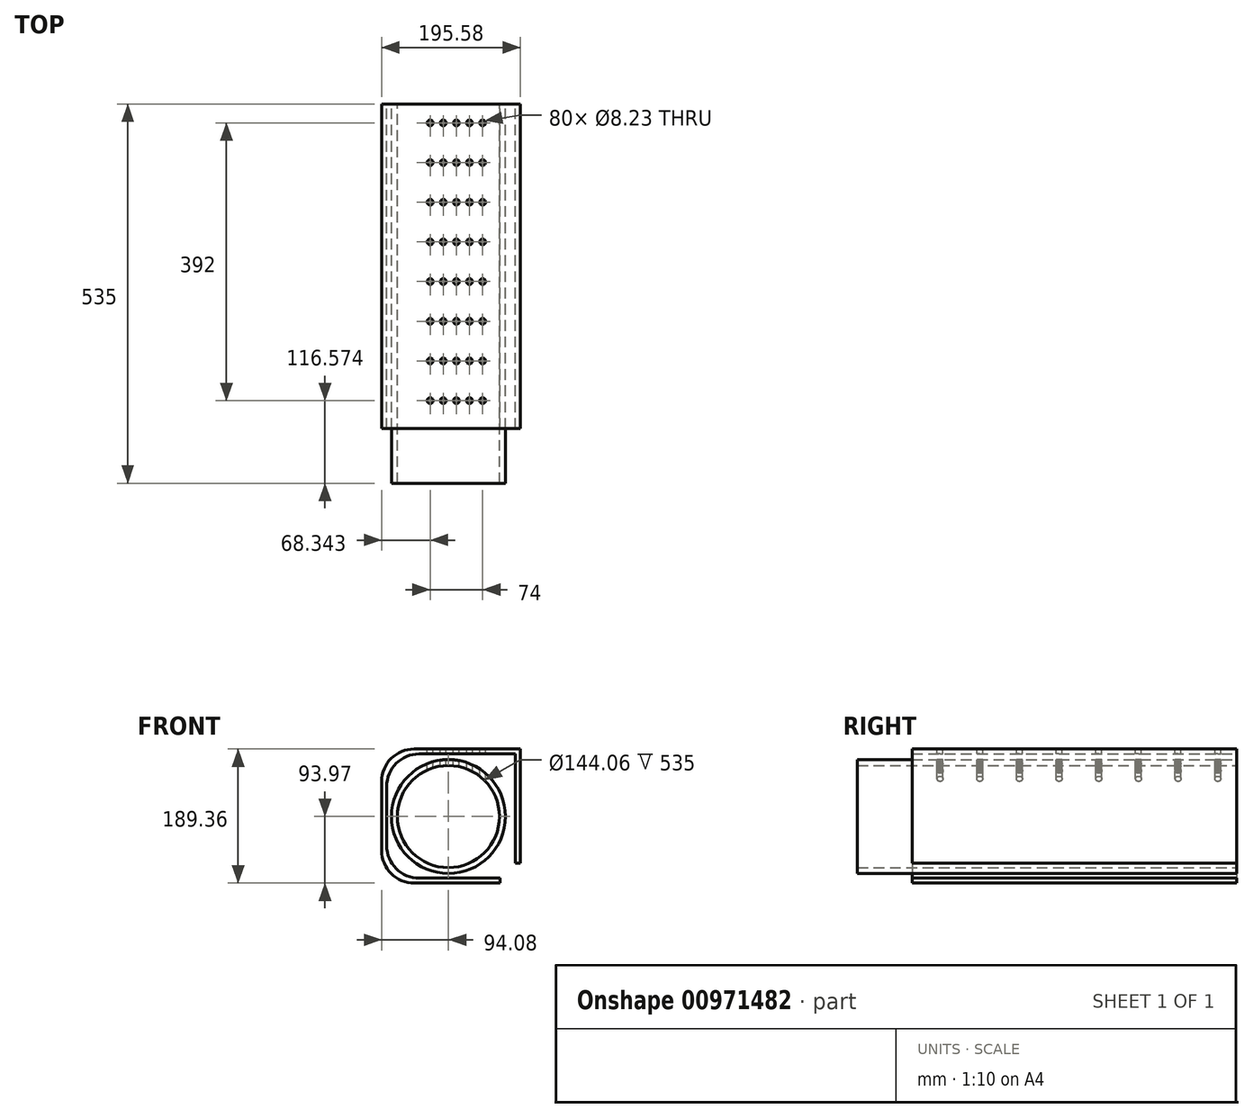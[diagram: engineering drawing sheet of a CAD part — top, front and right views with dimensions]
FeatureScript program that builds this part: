
annotation { "Feature Type Name" : "Feature", "Feature Type Description" : "" }
export const myFeature = defineFeature(function(context is Context, id is Id, definition is map)
    precondition{}
    {
        {
            var Q0;
            Q0=qCreatedBy(makeId("Front.planeOp"),FACE);
            var sketch = newSketch(context, id + "F0", { "sketchPlane" : qUnion([Q0])});
            skCircle(sketch, "E0", {"center": v(0, 0) * mm, "radius": 80.4 * mm});
            skCircle(sketch, "E1", {"center": v(0, 0) * mm, "radius": 72.03 * mm});
            skSolve(sketch);
        }
        {
            var Q0;
            Q0=makeQuery(id+"F0.imprint","IMPRINT",FACE,{"disambiguationData":[TD([[makeQuery(id+"F0.imprint","IMPRINT",EDGE,{"derivedFrom":sQuery(id+"F0.wireOp",EDGE,"E0")}),1.0]])]});
            extrude(context, id + "F1", {"entities" : qUnion([Q0]), "depth" : 535 * mm, "offsetDistance" : 25 * mm});
        }
        {
            var Q0;
            Q0=qCreatedBy(makeId("Front.planeOp"),FACE);
            var sketch = newSketch(context, id + "F2", { "sketchPlane" : qUnion([Q0])});
            skLineSegment(sketch, "E2.bottom", {"start": v(94.5, 88.4) * mm, "end": v(-87.08, 88.4) * mm});
            skLineSegment(sketch, "E2.top", {"start": v(94.5, -86.97) * mm, "end": v(-87.08, -86.97) * mm});
            skLineSegment(sketch, "E2.left", {"start": v(94.5, 88.4) * mm, "end": v(94.5, -86.97) * mm});
            skLineSegment(sketch, "E2.right", {"start": v(-87.08, 88.4) * mm, "end": v(-87.08, -86.97) * mm});
            skLineSegment(sketch, "E3.0", {"start": v(101.5, 95.4) * mm, "end": v(-94.08, 95.4) * mm});
            skLineSegment(sketch, "E3.1", {"start": v(101.5, 95.4) * mm, "end": v(101.5, -93.97) * mm});
            skLineSegment(sketch, "E3.2", {"start": v(101.5, -93.97) * mm, "end": v(-94.08, -93.97) * mm});
            skLineSegment(sketch, "E3.3", {"start": v(-94.08, 95.4) * mm, "end": v(-94.08, -93.97) * mm});
            skSolve(sketch);
        }
        {
            var Q0;
            Q0=makeQuery(id+"F2.imprint","IMPRINT",FACE,{"disambiguationData":[TD([[makeQuery(id+"F2.imprint","IMPRINT",EDGE,{"derivedFrom":sQuery(id+"F2.wireOp",EDGE,"E2.bottom")}),-1.0]])]});
            extrude(context, id + "F3", {"entities" : qUnion([Q0]), "depth" : 458 * mm, "offsetDistance" : 25 * mm});
        }
        {
            var Q0;
            Q0=makeQuery(id+"F3.opExtrude","SWEPT_EDGE",EDGE,{"disambiguationData":[OSD([sQuery(id+"F2.wireOp",EDGE,"E2.bottom"),sQuery(id+"F2.wireOp",EDGE,"E2.right")])]});
            var Q1;
            Q1=makeQuery(id+"F3.opExtrude","SWEPT_EDGE",EDGE,{"disambiguationData":[OSD([sQuery(id+"F2.wireOp",EDGE,"E3.0"),sQuery(id+"F2.wireOp",EDGE,"E3.3")])]});
            var Q2;
            Q2=makeQuery(id+"F3.opExtrude","SWEPT_EDGE",EDGE,{"disambiguationData":[OSD([sQuery(id+"F2.wireOp",EDGE,"E2.top"),sQuery(id+"F2.wireOp",EDGE,"E2.right")])]});
            var Q3;
            Q3=makeQuery(id+"F3.opExtrude","SWEPT_EDGE",EDGE,{"disambiguationData":[OSD([sQuery(id+"F2.wireOp",EDGE,"E3.2"),sQuery(id+"F2.wireOp",EDGE,"E3.3")])]});
            fillet(context, id + "F4", {"entities" : qUnion([Q0, Q1, Q2, Q3]), "radius" : 45.87 * mm, "tangentPropagation" : true, "allowEdgeOverflow" : false});
        }
        {
            var Q0;
            Q0=makeQuery(id+"F3.opExtrude","SWEPT_FACE",FACE,{"disambiguationData":[OSD([sQuery(id+"F2.wireOp",EDGE,"E3.0")])]});
            var sketch = newSketch(context, id + "F5", { "sketchPlane" : qUnion([Q0])});
            skCircle(sketch, "E4", {"center": v(-25.74, -26.43) * mm, "radius": 4.12 * mm});
            skCircle(sketch, "E5.0.1.0", {"center": v(-25.74, -82.43) * mm, "radius": 4.12 * mm});
            skCircle(sketch, "E5.0.2.0", {"center": v(-25.74, -138.43) * mm, "radius": 4.12 * mm});
            skCircle(sketch, "E5.0.3.0", {"center": v(-25.74, -194.43) * mm, "radius": 4.12 * mm});
            skCircle(sketch, "E5.0.4.0", {"center": v(-25.74, -250.43) * mm, "radius": 4.12 * mm});
            skCircle(sketch, "E5.0.5.0", {"center": v(-25.74, -306.43) * mm, "radius": 4.12 * mm});
            skCircle(sketch, "E5.0.6.0", {"center": v(-25.74, -362.43) * mm, "radius": 4.12 * mm});
            skCircle(sketch, "E5.0.7.0", {"center": v(-25.74, -418.43) * mm, "radius": 4.12 * mm});
            skCircle(sketch, "E5.1.0.0", {"center": v(-7.24, -26.43) * mm, "radius": 4.12 * mm});
            skCircle(sketch, "E5.1.1.0", {"center": v(-7.24, -82.43) * mm, "radius": 4.12 * mm});
            skCircle(sketch, "E5.1.2.0", {"center": v(-7.24, -138.43) * mm, "radius": 4.12 * mm});
            skCircle(sketch, "E5.1.3.0", {"center": v(-7.24, -194.43) * mm, "radius": 4.12 * mm});
            skCircle(sketch, "E5.1.4.0", {"center": v(-7.24, -250.43) * mm, "radius": 4.12 * mm});
            skCircle(sketch, "E5.1.5.0", {"center": v(-7.24, -306.43) * mm, "radius": 4.12 * mm});
            skCircle(sketch, "E5.1.6.0", {"center": v(-7.24, -362.43) * mm, "radius": 4.12 * mm});
            skCircle(sketch, "E5.1.7.0", {"center": v(-7.24, -418.43) * mm, "radius": 4.12 * mm});
            skCircle(sketch, "E5.2.0.0", {"center": v(11.26, -26.43) * mm, "radius": 4.12 * mm});
            skCircle(sketch, "E5.2.1.0", {"center": v(11.26, -82.43) * mm, "radius": 4.12 * mm});
            skCircle(sketch, "E5.2.2.0", {"center": v(11.26, -138.43) * mm, "radius": 4.12 * mm});
            skCircle(sketch, "E5.2.3.0", {"center": v(11.26, -194.43) * mm, "radius": 4.12 * mm});
            skCircle(sketch, "E5.2.4.0", {"center": v(11.26, -250.43) * mm, "radius": 4.12 * mm});
            skCircle(sketch, "E5.2.5.0", {"center": v(11.26, -306.43) * mm, "radius": 4.12 * mm});
            skCircle(sketch, "E5.2.6.0", {"center": v(11.26, -362.43) * mm, "radius": 4.12 * mm});
            skCircle(sketch, "E5.2.7.0", {"center": v(11.26, -418.43) * mm, "radius": 4.12 * mm});
            skCircle(sketch, "E5.3.0.0", {"center": v(29.76, -26.43) * mm, "radius": 4.12 * mm});
            skCircle(sketch, "E5.3.1.0", {"center": v(29.76, -82.43) * mm, "radius": 4.12 * mm});
            skCircle(sketch, "E5.3.2.0", {"center": v(29.76, -138.43) * mm, "radius": 4.12 * mm});
            skCircle(sketch, "E5.3.3.0", {"center": v(29.76, -194.43) * mm, "radius": 4.12 * mm});
            skCircle(sketch, "E5.3.4.0", {"center": v(29.76, -250.43) * mm, "radius": 4.12 * mm});
            skCircle(sketch, "E5.3.5.0", {"center": v(29.76, -306.43) * mm, "radius": 4.12 * mm});
            skCircle(sketch, "E5.3.6.0", {"center": v(29.76, -362.43) * mm, "radius": 4.12 * mm});
            skCircle(sketch, "E5.3.7.0", {"center": v(29.76, -418.43) * mm, "radius": 4.12 * mm});
            skCircle(sketch, "E5.4.0.0", {"center": v(48.26, -26.43) * mm, "radius": 4.12 * mm});
            skCircle(sketch, "E5.4.1.0", {"center": v(48.26, -82.43) * mm, "radius": 4.12 * mm});
            skCircle(sketch, "E5.4.2.0", {"center": v(48.26, -138.43) * mm, "radius": 4.12 * mm});
            skCircle(sketch, "E5.4.3.0", {"center": v(48.26, -194.43) * mm, "radius": 4.12 * mm});
            skCircle(sketch, "E5.4.4.0", {"center": v(48.26, -250.43) * mm, "radius": 4.12 * mm});
            skCircle(sketch, "E5.4.5.0", {"center": v(48.26, -306.43) * mm, "radius": 4.12 * mm});
            skCircle(sketch, "E5.4.6.0", {"center": v(48.26, -362.43) * mm, "radius": 4.12 * mm});
            skCircle(sketch, "E5.4.7.0", {"center": v(48.26, -418.43) * mm, "radius": 4.12 * mm});
            skLineSegment(sketch, "E5.direction1", {"start": v(-25.74, -26.43) * mm, "end": v(-7.24, -26.43) * mm, "construction": true});
            skLineSegment(sketch, "E5.direction2", {"start": v(-25.74, -26.43) * mm, "end": v(-25.74, -82.43) * mm, "construction": true});
            skSolve(sketch);
        }
        {
            var Q0;
            Q0 = qSketchRegion(id + "F5", true);
            extrude(context, id + "F6", {"entities" : qUnion([Q0]), "operationType" : NewBodyOperationType.REMOVE, "oppositeDirection" : true, "depth" : 56 * mm, "offsetDistance" : 25 * mm});
        }
        {
            var Q0;
            Q0=makeQuery(id+"F3.opExtrude","CAP_FACE",FACE,{"disambiguationData":[OSD([sQuery(id+"F2.wireOp",EDGE,"E2.bottom"),sQuery(id+"F2.wireOp",EDGE,"E2.top"),sQuery(id+"F2.wireOp",EDGE,"E2.left"),sQuery(id+"F2.wireOp",EDGE,"E2.right"),sQuery(id+"F2.wireOp",EDGE,"E3.0"),sQuery(id+"F2.wireOp",EDGE,"E3.2"),sQuery(id+"F2.wireOp",EDGE,"E3.1"),sQuery(id+"F2.wireOp",EDGE,"E3.3")])],"isStart":true});
            var sketch = newSketch(context, id + "F7", { "sketchPlane" : qUnion([Q0])});
            skLineSegment(sketch, "E6.bottom", {"start": v(-142.27, -112.12) * mm, "end": v(-72.82, -112.12) * mm});
            skLineSegment(sketch, "E6.top", {"start": v(-142.27, -65.56) * mm, "end": v(-72.82, -65.56) * mm});
            skLineSegment(sketch, "E6.left", {"start": v(-142.27, -112.12) * mm, "end": v(-142.27, -65.56) * mm});
            skLineSegment(sketch, "E6.right", {"start": v(-72.82, -112.12) * mm, "end": v(-72.82, -65.56) * mm});
            skSolve(sketch);
        }
        {
            var Q0;
            {var subQ1=makeQuery(id+"F3.opExtrude","CAP_EDGE",EDGE,{"disambiguationData":[OSD([sQuery(id+"F2.wireOp",EDGE,"E3.1")])],"isStart":true});var subQ3=sQuery(id+"F7.wireOp",EDGE,"E6.top");var subQ4=makeQuery(id+"F7.imprint","INTERSECT",VERTEX,{"derivedFrom":[subQ1,subQ3]});Q0=makeQuery(id+"F7.imprint","IMPRINT",FACE,{"disambiguationData":[TD([[makeQuery(id+"F7.imprint","IMPRINT",EDGE,{"disambiguationData":[TD([[subQ4,-1.0]])],"derivedFrom":subQ3}),-1.0]])]});}
            var Q1;
            {var subQ0=sQuery(id+"F7.wireOp",EDGE,"E6.right");var subQ1=sQuery(id+"F7.wireOp",EDGE,"E6.top");var subQ2=makeQuery(id+"F7.imprint","INTERSECT",VERTEX,{"derivedFrom":[subQ1,subQ0]});Q1=makeQuery(id+"F7.imprint","IMPRINT",FACE,{"disambiguationData":[TD([[makeQuery(id+"F7.imprint","IMPRINT",EDGE,{"disambiguationData":[TD([[subQ2,1.0]])],"derivedFrom":subQ1}),-1.0]])]});}
            var Q2;
            {var subQ8=sQuery(id+"F7.wireOp",EDGE,"E6.bottom");Q2=makeQuery(id+"F7.imprint","IMPRINT",FACE,{"disambiguationData":[TD([[makeQuery(id+"F7.imprint","IMPRINT",EDGE,{"derivedFrom":subQ8}),1.0]])]});}
            extrude(context, id + "F8", {"entities" : qUnion([Q0, Q1, Q2]), "operationType" : NewBodyOperationType.REMOVE, "oppositeDirection" : true, "depth" : 939 * mm, "offsetDistance" : 25 * mm});
        }
    });
